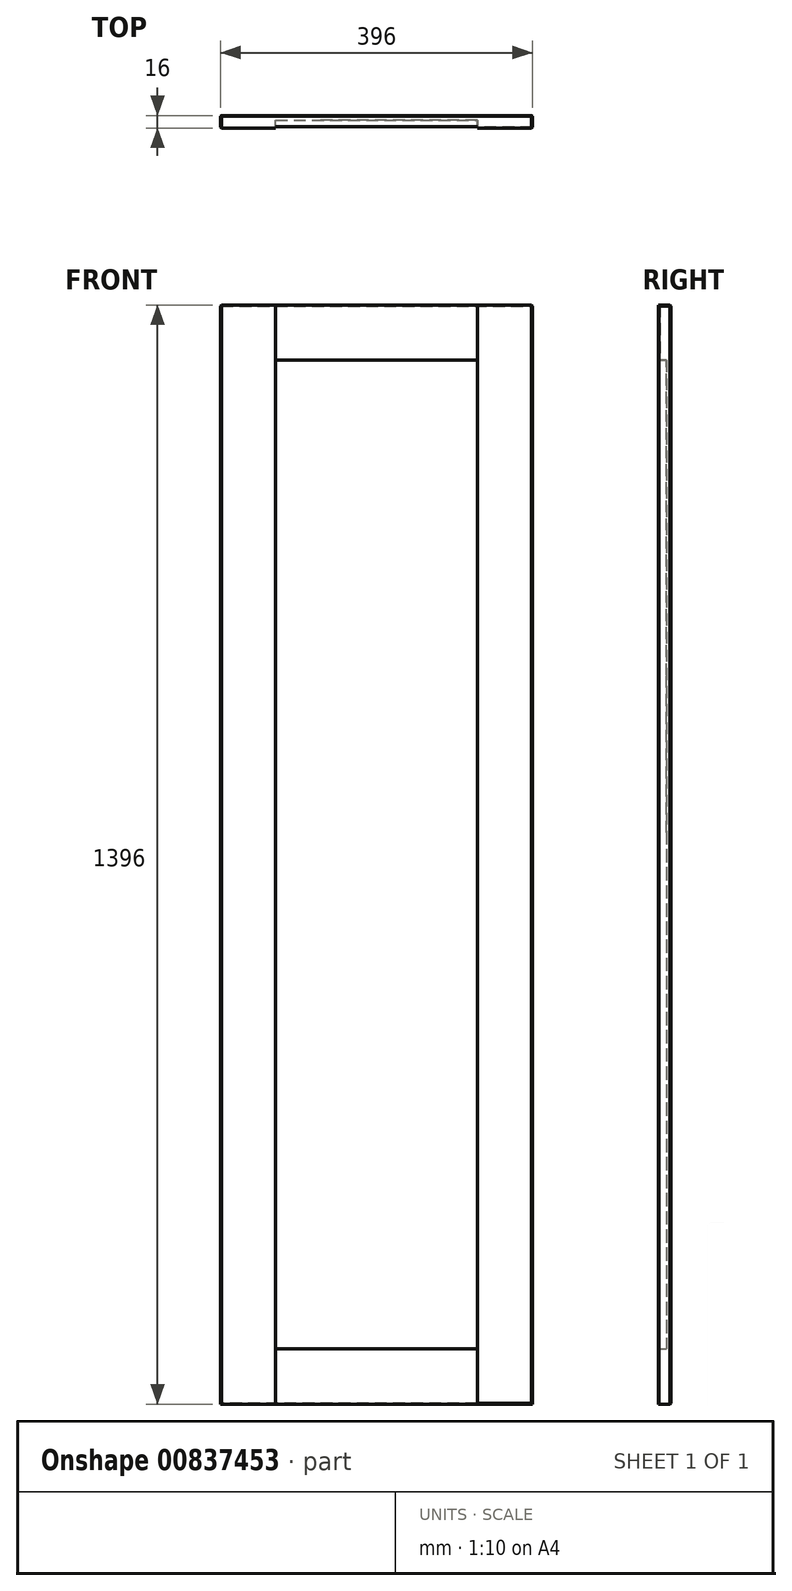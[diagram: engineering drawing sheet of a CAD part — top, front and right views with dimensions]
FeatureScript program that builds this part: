
annotation { "Feature Type Name" : "Feature", "Feature Type Description" : "" }
export const myFeature = defineFeature(function(context is Context, id is Id, definition is map)
    precondition{}
    {
        {
            var Q0;
            Q0=qCreatedBy(makeId("Front.planeOp"),FACE);
            var sketch = newSketch(context, id + "F0", { "sketchPlane" : qUnion([Q0])});
            skLineSegment(sketch, "E0.bottom", {"start": v(0, 0) * mm, "end": v(35.9, 0) * mm});
            skLineSegment(sketch, "E0.top", {"start": v(0, 30.12) * mm, "end": v(35.9, 30.12) * mm});
            skLineSegment(sketch, "E0.left", {"start": v(0, 0) * mm, "end": v(0, 30.12) * mm});
            skLineSegment(sketch, "E0.right", {"start": v(35.9, 0) * mm, "end": v(35.9, 30.12) * mm});
            skSolve(sketch);
        }
        {
            var Q0;
            Q0=makeQuery(id+"F0.imprint","IMPRINT",FACE,{"disambiguationData":[TD([[makeQuery(id+"F0.imprint","IMPRINT",EDGE,{"derivedFrom":sQuery(id+"F0.wireOp",EDGE,"E0.bottom")}),1.0]])]});
            extrude(context, id + "F1", {"entities" : qUnion([Q0]), "depth" : 16 * mm, "offsetDistance" : 25.4 * mm});
        }
        {
            var Q0;
            Q0=makeQuery(id+"F1.opExtrude","SWEPT_FACE",FACE,{"disambiguationData":[OSD([sQuery(id+"F0.wireOp",EDGE,"E0.left")])]});
            extrude(context, id + "F2", {"entities" : qUnion([Q0]), "operationType" : NewBodyOperationType.ADD, "oppositeDirection" : true, "depth" : 196 * mm, "offsetDistance" : 25 * mm});
        }
        {
            var Q0;
            {var subQ0=sQuery(id+"F0.wireOp",EDGE,"E0.bottom");Q0=makeQuery(id+"F2.boolean.opBoolean","MERGE",FACE,{"derivedFrom":[makeQuery(id+"F1.opExtrude","SWEPT_FACE",FACE,{"disambiguationData":[OSD([subQ0])]}),makeQuery(id+"F2.opExtrude","SWEPT_FACE",FACE,{"disambiguationData":[OSD([subQ0,sQuery(id+"F0.wireOp",EDGE,"E0.left")])]})]});}
            extrude(context, id + "F3", {"entities" : qUnion([Q0]), "operationType" : NewBodyOperationType.ADD, "oppositeDirection" : true, "depth" : 796 * mm, "offsetDistance" : 25 * mm});
        }
        {
            var Q0;
            {var subQ0=sQuery(id+"F0.wireOp",EDGE,"E0.left");var subQ1=sQuery(id+"F0.wireOp",EDGE,"E0.bottom");Q0=makeQuery(id+"F3.boolean.opBoolean","MERGE",FACE,{"derivedFrom":[makeQuery(id+"F2.boolean.opBoolean","MERGE",FACE,{"derivedFrom":[makeQuery(id+"F1.opExtrude","CAP_FACE",FACE,{"disambiguationData":[OSD([subQ1,sQuery(id+"F0.wireOp",EDGE,"E0.top"),subQ0,sQuery(id+"F0.wireOp",EDGE,"E0.right")])],"isStart":false}),makeQuery(id+"F2.opExtrude","SWEPT_FACE",FACE,{"disambiguationData":[OSD([subQ0]),TDD([makeQuery(id+"F1.opExtrude","CAP_EDGE",EDGE,{"disambiguationData":[OSD([subQ0])],"isStart":false})])]})]}),makeQuery(id+"F3.opExtrude","SWEPT_FACE",FACE,{"disambiguationData":[OSD([subQ1,subQ0]),TDD([makeQuery(id+"F2.boolean.opBoolean","MERGE",EDGE,{"derivedFrom":[makeQuery(id+"F1.opExtrude","CAP_EDGE",EDGE,{"disambiguationData":[OSD([subQ1])],"isStart":false}),makeQuery(id+"F2.opExtrude","SWEPT_EDGE",EDGE,{"disambiguationData":[OSD([subQ1,subQ0]),TDD([makeQuery(id+"F1.opExtrude","CAP_VERTEX",VERTEX,{"disambiguationData":[OSD([subQ1,subQ0])],"isStart":false})])]})]})])]})]});}
            var sketch = newSketch(context, id + "F4", { "sketchPlane" : qUnion([Q0])});
            skLineSegment(sketch, "E1.bottom", {"start": v(0, 796) * mm, "end": v(42.19, 796) * mm});
            skLineSegment(sketch, "E1.top", {"start": v(0, 751.57) * mm, "end": v(42.19, 751.57) * mm});
            skLineSegment(sketch, "E1.left", {"start": v(0, 796) * mm, "end": v(0, 751.57) * mm});
            skLineSegment(sketch, "E1.right", {"start": v(42.19, 796) * mm, "end": v(42.19, 751.57) * mm});
            skLineSegment(sketch, "E2.bottom", {"start": v(196, 796) * mm, "end": v(153.6, 796) * mm});
            skLineSegment(sketch, "E2.top", {"start": v(196, 746.75) * mm, "end": v(153.6, 746.75) * mm});
            skLineSegment(sketch, "E2.left", {"start": v(196, 796) * mm, "end": v(196, 746.75) * mm});
            skLineSegment(sketch, "E2.right", {"start": v(153.6, 796) * mm, "end": v(153.6, 746.75) * mm});
            skSolve(sketch);
        }
        {
            var Q0;
            Q0=makeQuery(id+"F4.imprint","IMPRINT",FACE,{"disambiguationData":[TD([[makeQuery(id+"F4.imprint","IMPRINT",EDGE,{"derivedFrom":sQuery(id+"F4.wireOp",EDGE,"E1.bottom")}),-1.0]])]});
            var Q1;
            Q1=makeQuery(id+"F4.imprint","IMPRINT",FACE,{"disambiguationData":[TD([[makeQuery(id+"F4.imprint","IMPRINT",EDGE,{"derivedFrom":sQuery(id+"F4.wireOp",EDGE,"E2.bottom")}),-1.0]])]});
            extrude(context, id + "F5", {"entities" : qUnion([Q0, Q1]), "operationType" : NewBodyOperationType.ADD, "depth" : 25 * mm, "offsetDistance" : 25 * mm});
        }
        {
            var Q0;
            {var subQ0=sQuery(id+"F0.wireOp",EDGE,"E0.left");var subQ1=sQuery(id+"F0.wireOp",EDGE,"E0.bottom");Q0=makeQuery(id+"F3.boolean.opBoolean","MERGE",FACE,{"derivedFrom":[makeQuery(id+"F2.boolean.opBoolean","MERGE",FACE,{"derivedFrom":[makeQuery(id+"F1.opExtrude","CAP_FACE",FACE,{"disambiguationData":[OSD([subQ1,sQuery(id+"F0.wireOp",EDGE,"E0.top"),subQ0,sQuery(id+"F0.wireOp",EDGE,"E0.right")])],"isStart":false}),makeQuery(id+"F2.opExtrude","SWEPT_FACE",FACE,{"disambiguationData":[OSD([subQ0]),TDD([makeQuery(id+"F1.opExtrude","CAP_EDGE",EDGE,{"disambiguationData":[OSD([subQ0])],"isStart":false})])]})]}),makeQuery(id+"F3.opExtrude","SWEPT_FACE",FACE,{"disambiguationData":[OSD([subQ1,subQ0]),TDD([makeQuery(id+"F2.boolean.opBoolean","MERGE",EDGE,{"derivedFrom":[makeQuery(id+"F1.opExtrude","CAP_EDGE",EDGE,{"disambiguationData":[OSD([subQ1])],"isStart":false}),makeQuery(id+"F2.opExtrude","SWEPT_EDGE",EDGE,{"disambiguationData":[OSD([subQ1,subQ0]),TDD([makeQuery(id+"F1.opExtrude","CAP_VERTEX",VERTEX,{"disambiguationData":[OSD([subQ1,subQ0])],"isStart":false})])]})]})])]})]});}
            var sketch = newSketch(context, id + "F6", { "sketchPlane" : qUnion([Q0])});
            skLineSegment(sketch, "E3.bottom", {"start": v(196, 0) * mm, "end": v(163.38, 0) * mm});
            skLineSegment(sketch, "E3.top", {"start": v(196, 46.55) * mm, "end": v(163.38, 46.55) * mm});
            skLineSegment(sketch, "E3.left", {"start": v(196, 0) * mm, "end": v(196, 46.55) * mm});
            skLineSegment(sketch, "E3.right", {"start": v(163.38, 0) * mm, "end": v(163.38, 46.55) * mm});
            skLineSegment(sketch, "E4.bottom", {"start": v(0, 0) * mm, "end": v(50.28, 0) * mm});
            skLineSegment(sketch, "E4.top", {"start": v(0, 44.4) * mm, "end": v(50.28, 44.4) * mm});
            skLineSegment(sketch, "E4.left", {"start": v(0, 0) * mm, "end": v(0, 44.4) * mm});
            skLineSegment(sketch, "E4.right", {"start": v(50.28, 0) * mm, "end": v(50.28, 44.4) * mm});
            skSolve(sketch);
        }
        {
            var Q0;
            Q0=makeQuery(id+"F6.imprint","IMPRINT",FACE,{"disambiguationData":[TD([[makeQuery(id+"F6.imprint","IMPRINT",EDGE,{"derivedFrom":sQuery(id+"F6.wireOp",EDGE,"E3.bottom")}),1.0]])]});
            var Q1;
            Q1=makeQuery(id+"F6.imprint","IMPRINT",FACE,{"disambiguationData":[TD([[makeQuery(id+"F6.imprint","IMPRINT",EDGE,{"derivedFrom":sQuery(id+"F6.wireOp",EDGE,"E4.bottom")}),1.0]])]});
            extrude(context, id + "F7", {"entities" : qUnion([Q0, Q1]), "operationType" : NewBodyOperationType.ADD, "depth" : 25 * mm, "offsetDistance" : 25 * mm});
        }
        {
            var Q0;
            Q0=makeQuery(id+"F7.opExtrude","SWEPT_FACE",FACE,{"disambiguationData":[OSD([sQuery(id+"F6.wireOp",EDGE,"E4.right")])]});
            extrude(context, id + "F8", {"entities" : qUnion([Q0]), "operationType" : NewBodyOperationType.ADD, "depth" : 19.72 * mm, "offsetDistance" : 25 * mm});
        }
        {
            var Q0;
            {var subQ0=sQuery(id+"F6.wireOp",EDGE,"E4.top");Q0=makeQuery(id+"F8.boolean.opBoolean","MERGE",FACE,{"derivedFrom":[makeQuery(id+"F7.opExtrude","SWEPT_FACE",FACE,{"disambiguationData":[OSD([subQ0])]}),makeQuery(id+"F8.opExtrude","SWEPT_FACE",FACE,{"disambiguationData":[OSD([subQ0,sQuery(id+"F6.wireOp",EDGE,"E4.right")])]})]});}
            extrude(context, id + "F9", {"entities" : qUnion([Q0]), "operationType" : NewBodyOperationType.ADD, "depth" : 25.6 * mm, "offsetDistance" : 25 * mm});
        }
        {
            var Q0;
            Q0=makeQuery(id+"F7.opExtrude","SWEPT_FACE",FACE,{"disambiguationData":[OSD([sQuery(id+"F6.wireOp",EDGE,"E3.right")])]});
            extrude(context, id + "F10", {"entities" : qUnion([Q0]), "operationType" : NewBodyOperationType.ADD, "depth" : 37.38 * mm, "offsetDistance" : 25 * mm});
        }
        {
            var Q0;
            {var subQ0=sQuery(id+"F6.wireOp",EDGE,"E3.top");Q0=makeQuery(id+"F10.boolean.opBoolean","MERGE",FACE,{"derivedFrom":[makeQuery(id+"F7.opExtrude","SWEPT_FACE",FACE,{"disambiguationData":[OSD([subQ0])]}),makeQuery(id+"F10.opExtrude","SWEPT_FACE",FACE,{"disambiguationData":[OSD([subQ0,sQuery(id+"F6.wireOp",EDGE,"E3.right")])]})]});}
            extrude(context, id + "F11", {"entities" : qUnion([Q0]), "operationType" : NewBodyOperationType.ADD, "depth" : 23.45 * mm, "offsetDistance" : 25 * mm});
        }
        {
            var Q0;
            Q0=makeQuery(id+"F5.opExtrude","SWEPT_FACE",FACE,{"disambiguationData":[OSD([sQuery(id+"F4.wireOp",EDGE,"E1.right")])]});
            extrude(context, id + "F12", {"entities" : qUnion([Q0]), "operationType" : NewBodyOperationType.ADD, "depth" : 27.8 * mm, "offsetDistance" : 25 * mm});
        }
        {
            var Q0;
            {var subQ0=sQuery(id+"F4.wireOp",EDGE,"E1.top");Q0=makeQuery(id+"F12.boolean.opBoolean","MERGE",FACE,{"derivedFrom":[makeQuery(id+"F5.opExtrude","SWEPT_FACE",FACE,{"disambiguationData":[OSD([subQ0])]}),makeQuery(id+"F12.opExtrude","SWEPT_FACE",FACE,{"disambiguationData":[OSD([subQ0,sQuery(id+"F4.wireOp",EDGE,"E1.right")])]})]});}
            extrude(context, id + "F13", {"entities" : qUnion([Q0]), "operationType" : NewBodyOperationType.ADD, "depth" : 25.57 * mm, "offsetDistance" : 25 * mm});
        }
        {
            var Q0;
            Q0=makeQuery(id+"F5.opExtrude","SWEPT_FACE",FACE,{"disambiguationData":[OSD([sQuery(id+"F4.wireOp",EDGE,"E2.top")])]});
            extrude(context, id + "F14", {"entities" : qUnion([Q0]), "operationType" : NewBodyOperationType.ADD, "depth" : 20.75 * mm, "offsetDistance" : 25 * mm});
        }
        {
            var Q0;
            {var subQ0=sQuery(id+"F4.wireOp",EDGE,"E2.right");Q0=makeQuery(id+"F14.boolean.opBoolean","MERGE",FACE,{"derivedFrom":[makeQuery(id+"F5.opExtrude","SWEPT_FACE",FACE,{"disambiguationData":[OSD([subQ0])]}),makeQuery(id+"F14.opExtrude","SWEPT_FACE",FACE,{"disambiguationData":[OSD([sQuery(id+"F4.wireOp",EDGE,"E2.top"),subQ0])]})]});}
            extrude(context, id + "F15", {"entities" : qUnion([Q0]), "operationType" : NewBodyOperationType.ADD, "depth" : 27.6 * mm, "offsetDistance" : 25 * mm});
        }
        {
            var Q0;
            {var subQ0=sQuery(id+"F0.wireOp",EDGE,"E0.left");var subQ1=sQuery(id+"F0.wireOp",EDGE,"E0.bottom");Q0=makeQuery(id+"F3.boolean.opBoolean","MERGE",FACE,{"derivedFrom":[makeQuery(id+"F2.boolean.opBoolean","MERGE",FACE,{"derivedFrom":[makeQuery(id+"F1.opExtrude","CAP_FACE",FACE,{"disambiguationData":[OSD([subQ1,sQuery(id+"F0.wireOp",EDGE,"E0.top"),subQ0,sQuery(id+"F0.wireOp",EDGE,"E0.right")])],"isStart":false}),makeQuery(id+"F2.opExtrude","SWEPT_FACE",FACE,{"disambiguationData":[OSD([subQ0]),TDD([makeQuery(id+"F1.opExtrude","CAP_EDGE",EDGE,{"disambiguationData":[OSD([subQ0])],"isStart":false})])]})]}),makeQuery(id+"F3.opExtrude","SWEPT_FACE",FACE,{"disambiguationData":[OSD([subQ1,subQ0]),TDD([makeQuery(id+"F2.boolean.opBoolean","MERGE",EDGE,{"derivedFrom":[makeQuery(id+"F1.opExtrude","CAP_EDGE",EDGE,{"disambiguationData":[OSD([subQ1])],"isStart":false}),makeQuery(id+"F2.opExtrude","SWEPT_EDGE",EDGE,{"disambiguationData":[OSD([subQ1,subQ0]),TDD([makeQuery(id+"F1.opExtrude","CAP_VERTEX",VERTEX,{"disambiguationData":[OSD([subQ1,subQ0])],"isStart":false})])]})]})])]})]});}
            var sketch = newSketch(context, id + "F16", { "sketchPlane" : qUnion([Q0])});
            skLineSegment(sketch, "E5.bottom", {"start": v(70, 726) * mm, "end": v(126, 726) * mm});
            skLineSegment(sketch, "E5.top", {"start": v(70, 70) * mm, "end": v(126, 70) * mm});
            skLineSegment(sketch, "E5.left", {"start": v(70, 726) * mm, "end": v(70, 70) * mm});
            skLineSegment(sketch, "E5.right", {"start": v(126, 726) * mm, "end": v(126, 70) * mm});
            skSolve(sketch);
        }
        {
            var Q0;
            Q0=makeQuery(id+"F16.imprint","IMPRINT",FACE,{"disambiguationData":[TD([[makeQuery(id+"F16.imprint","IMPRINT",EDGE,{"derivedFrom":sQuery(id+"F16.wireOp",EDGE,"E5.top")}),1.0]])]});
            extrude(context, id + "F17", {"entities" : qUnion([Q0]), "operationType" : NewBodyOperationType.REMOVE, "oppositeDirection" : true, "depth" : 10 * mm, "offsetDistance" : 25 * mm});
        }
        {
            var Q0;
            {var subQ2=sQuery(id+"F0.wireOp",EDGE,"E0.left");var subQ3=sQuery(id+"F0.wireOp",EDGE,"E0.bottom");var subQ4=makeQuery(id+"F1.opExtrude","CAP_FACE",FACE,{"disambiguationData":[OSD([subQ3,sQuery(id+"F0.wireOp",EDGE,"E0.top"),subQ2,sQuery(id+"F0.wireOp",EDGE,"E0.right")])],"isStart":false});var subQ7=makeQuery(id+"F3.opExtrude","SWEPT_FACE",FACE,{"disambiguationData":[OSD([subQ3,subQ2]),TDD([makeQuery(id+"F2.boolean.opBoolean","MERGE",EDGE,{"derivedFrom":[makeQuery(id+"F1.opExtrude","CAP_EDGE",EDGE,{"disambiguationData":[OSD([subQ3])],"isStart":false}),makeQuery(id+"F2.opExtrude","SWEPT_EDGE",EDGE,{"disambiguationData":[OSD([subQ3,subQ2]),TDD([makeQuery(id+"F1.opExtrude","CAP_VERTEX",VERTEX,{"disambiguationData":[OSD([subQ3,subQ2])],"isStart":false})])]})]})])]});var subQ8=makeQuery(id+"F2.opExtrude","SWEPT_FACE",FACE,{"disambiguationData":[OSD([subQ2]),TDD([makeQuery(id+"F1.opExtrude","CAP_EDGE",EDGE,{"disambiguationData":[OSD([subQ2])],"isStart":false})])]});Q0=makeQuery(id+"F17.boolean.opBoolean","SPLIT",FACE,{"disambiguationData":[TD([makeQuery(id+"F1.opExtrude","SWEPT_FACE",FACE,{"disambiguationData":[OSD([subQ3])]})])],"derivedFrom":makeQuery(id+"F3.boolean.opBoolean","MERGE",FACE,{"derivedFrom":[makeQuery(id+"F2.boolean.opBoolean","MERGE",FACE,{"derivedFrom":[subQ4,subQ8]}),subQ7]})});}
            var Q1;
            {var subQ2=sQuery(id+"F4.wireOp",EDGE,"E1.bottom");var subQ3=sQuery(id+"F0.wireOp",EDGE,"E0.left");var subQ4=sQuery(id+"F0.wireOp",EDGE,"E0.bottom");var subQ6=makeQuery(id+"F1.opExtrude","CAP_FACE",FACE,{"disambiguationData":[OSD([subQ4,sQuery(id+"F0.wireOp",EDGE,"E0.top"),subQ3,sQuery(id+"F0.wireOp",EDGE,"E0.right")])],"isStart":false});var subQ7=makeQuery(id+"F2.opExtrude","SWEPT_FACE",FACE,{"disambiguationData":[OSD([subQ3]),TDD([makeQuery(id+"F1.opExtrude","CAP_EDGE",EDGE,{"disambiguationData":[OSD([subQ3])],"isStart":false})])]});var subQ8=makeQuery(id+"F3.opExtrude","SWEPT_FACE",FACE,{"disambiguationData":[OSD([subQ4,subQ3]),TDD([makeQuery(id+"F2.boolean.opBoolean","MERGE",EDGE,{"derivedFrom":[makeQuery(id+"F1.opExtrude","CAP_EDGE",EDGE,{"disambiguationData":[OSD([subQ4])],"isStart":false}),makeQuery(id+"F2.opExtrude","SWEPT_EDGE",EDGE,{"disambiguationData":[OSD([subQ4,subQ3]),TDD([makeQuery(id+"F1.opExtrude","CAP_VERTEX",VERTEX,{"disambiguationData":[OSD([subQ4,subQ3])],"isStart":false})])]})]})])]});Q1=makeQuery(id+"F17.boolean.opBoolean","SPLIT",FACE,{"disambiguationData":[TD([makeQuery(id+"F5.opExtrude","SWEPT_FACE",FACE,{"disambiguationData":[OSD([subQ2])]})])],"derivedFrom":makeQuery(id+"F3.boolean.opBoolean","MERGE",FACE,{"derivedFrom":[makeQuery(id+"F2.boolean.opBoolean","MERGE",FACE,{"derivedFrom":[subQ6,subQ7]}),subQ8]})});}
            extrude(context, id + "F18", {"entities" : qUnion([Q0, Q1]), "operationType" : NewBodyOperationType.REMOVE, "oppositeDirection" : true, "depth" : 2 * mm, "offsetDistance" : 25 * mm});
        }
        {
            var Q0;
            {var subQ0=sQuery(id+"F4.wireOp",EDGE,"E1.right");var subQ1=sQuery(id+"F4.wireOp",EDGE,"E1.top");Q0=makeQuery(id+"F13.boolean.opBoolean","MERGE",FACE,{"derivedFrom":[makeQuery(id+"F12.boolean.opBoolean","MERGE",FACE,{"derivedFrom":[makeQuery(id+"F5.opExtrude","CAP_FACE",FACE,{"disambiguationData":[OSD([sQuery(id+"F4.wireOp",EDGE,"E1.bottom"),subQ1,sQuery(id+"F4.wireOp",EDGE,"E1.left"),subQ0])],"isStart":false}),makeQuery(id+"F12.opExtrude","SWEPT_FACE",FACE,{"disambiguationData":[OSD([subQ0]),TDD([makeQuery(id+"F5.opExtrude","CAP_EDGE",EDGE,{"disambiguationData":[OSD([subQ0])],"isStart":false})])]})]}),makeQuery(id+"F13.opExtrude","SWEPT_FACE",FACE,{"disambiguationData":[OSD([subQ1,subQ0]),TDD([makeQuery(id+"F12.boolean.opBoolean","MERGE",EDGE,{"derivedFrom":[makeQuery(id+"F5.opExtrude","CAP_EDGE",EDGE,{"disambiguationData":[OSD([subQ1])],"isStart":false}),makeQuery(id+"F12.opExtrude","SWEPT_EDGE",EDGE,{"disambiguationData":[OSD([subQ1,subQ0]),TDD([makeQuery(id+"F5.opExtrude","CAP_VERTEX",VERTEX,{"disambiguationData":[OSD([subQ1,subQ0])],"isStart":false})])]})]})])]})]});}
            var Q1;
            {var subQ0=sQuery(id+"F4.wireOp",EDGE,"E2.right");var subQ1=sQuery(id+"F4.wireOp",EDGE,"E2.top");Q1=makeQuery(id+"F15.boolean.opBoolean","MERGE",FACE,{"derivedFrom":[makeQuery(id+"F14.boolean.opBoolean","MERGE",FACE,{"derivedFrom":[makeQuery(id+"F5.opExtrude","CAP_FACE",FACE,{"disambiguationData":[OSD([sQuery(id+"F4.wireOp",EDGE,"E2.bottom"),subQ1,sQuery(id+"F4.wireOp",EDGE,"E2.left"),subQ0])],"isStart":false}),makeQuery(id+"F14.opExtrude","SWEPT_FACE",FACE,{"disambiguationData":[OSD([subQ1]),TDD([makeQuery(id+"F5.opExtrude","CAP_EDGE",EDGE,{"disambiguationData":[OSD([subQ1])],"isStart":false})])]})]}),makeQuery(id+"F15.opExtrude","SWEPT_FACE",FACE,{"disambiguationData":[OSD([subQ1,subQ0]),TDD([makeQuery(id+"F14.boolean.opBoolean","MERGE",EDGE,{"derivedFrom":[makeQuery(id+"F5.opExtrude","CAP_EDGE",EDGE,{"disambiguationData":[OSD([subQ0])],"isStart":false}),makeQuery(id+"F14.opExtrude","SWEPT_EDGE",EDGE,{"disambiguationData":[OSD([subQ1,subQ0]),TDD([makeQuery(id+"F5.opExtrude","CAP_VERTEX",VERTEX,{"disambiguationData":[OSD([subQ1,subQ0])],"isStart":false})])]})]})])]})]});}
            var Q2;
            {var subQ0=sQuery(id+"F6.wireOp",EDGE,"E4.right");var subQ1=sQuery(id+"F6.wireOp",EDGE,"E4.top");Q2=makeQuery(id+"F9.boolean.opBoolean","MERGE",FACE,{"derivedFrom":[makeQuery(id+"F8.boolean.opBoolean","MERGE",FACE,{"derivedFrom":[makeQuery(id+"F7.opExtrude","CAP_FACE",FACE,{"disambiguationData":[OSD([sQuery(id+"F6.wireOp",EDGE,"E4.bottom"),subQ1,sQuery(id+"F6.wireOp",EDGE,"E4.left"),subQ0])],"isStart":false}),makeQuery(id+"F8.opExtrude","SWEPT_FACE",FACE,{"disambiguationData":[OSD([subQ0]),TDD([makeQuery(id+"F7.opExtrude","CAP_EDGE",EDGE,{"disambiguationData":[OSD([subQ0])],"isStart":false})])]})]}),makeQuery(id+"F9.opExtrude","SWEPT_FACE",FACE,{"disambiguationData":[OSD([subQ1,subQ0]),TDD([makeQuery(id+"F8.boolean.opBoolean","MERGE",EDGE,{"derivedFrom":[makeQuery(id+"F7.opExtrude","CAP_EDGE",EDGE,{"disambiguationData":[OSD([subQ1])],"isStart":false}),makeQuery(id+"F8.opExtrude","SWEPT_EDGE",EDGE,{"disambiguationData":[OSD([subQ1,subQ0]),TDD([makeQuery(id+"F7.opExtrude","CAP_VERTEX",VERTEX,{"disambiguationData":[OSD([subQ1,subQ0])],"isStart":false})])]})]})])]})]});}
            var Q3;
            {var subQ0=sQuery(id+"F6.wireOp",EDGE,"E3.right");var subQ1=sQuery(id+"F6.wireOp",EDGE,"E3.top");Q3=makeQuery(id+"F11.boolean.opBoolean","MERGE",FACE,{"derivedFrom":[makeQuery(id+"F10.boolean.opBoolean","MERGE",FACE,{"derivedFrom":[makeQuery(id+"F7.opExtrude","CAP_FACE",FACE,{"disambiguationData":[OSD([sQuery(id+"F6.wireOp",EDGE,"E3.bottom"),subQ1,sQuery(id+"F6.wireOp",EDGE,"E3.left"),subQ0])],"isStart":false}),makeQuery(id+"F10.opExtrude","SWEPT_FACE",FACE,{"disambiguationData":[OSD([subQ0]),TDD([makeQuery(id+"F7.opExtrude","CAP_EDGE",EDGE,{"disambiguationData":[OSD([subQ0])],"isStart":false})])]})]}),makeQuery(id+"F11.opExtrude","SWEPT_FACE",FACE,{"disambiguationData":[OSD([subQ1,subQ0]),TDD([makeQuery(id+"F10.boolean.opBoolean","MERGE",EDGE,{"derivedFrom":[makeQuery(id+"F7.opExtrude","CAP_EDGE",EDGE,{"disambiguationData":[OSD([subQ1])],"isStart":false}),makeQuery(id+"F10.opExtrude","SWEPT_EDGE",EDGE,{"disambiguationData":[OSD([subQ1,subQ0]),TDD([makeQuery(id+"F7.opExtrude","CAP_VERTEX",VERTEX,{"disambiguationData":[OSD([subQ1,subQ0])],"isStart":false})])]})]})])]})]});}
            extrude(context, id + "F19", {"entities" : qUnion([Q0, Q1, Q2, Q3]), "operationType" : NewBodyOperationType.REMOVE, "oppositeDirection" : true, "depth" : 25 * mm, "offsetDistance" : 25 * mm});
        }
        {
            var Q0;
            {var subQ0=sQuery(id+"F4.wireOp",EDGE,"E2.left");var subQ1=sQuery(id+"F0.wireOp",EDGE,"E0.left");var subQ2=sQuery(id+"F0.wireOp",EDGE,"E0.bottom");var subQ3=sQuery(id+"F6.wireOp",EDGE,"E3.left");Q0=makeQuery(id+"F14.boolean.opBoolean","MERGE",FACE,{"derivedFrom":[makeQuery(id+"F11.boolean.opBoolean","MERGE",FACE,{"derivedFrom":[makeQuery(id+"F7.boolean.opBoolean","MERGE",FACE,{"derivedFrom":[makeQuery(id+"F5.boolean.opBoolean","MERGE",FACE,{"derivedFrom":[makeQuery(id+"F3.boolean.opBoolean","MERGE",FACE,{"derivedFrom":[makeQuery(id+"F2.opExtrude","CAP_FACE",FACE,{"disambiguationData":[OSD([subQ1])],"isStart":false}),makeQuery(id+"F3.opExtrude","SWEPT_FACE",FACE,{"disambiguationData":[OSD([subQ2,subQ1]),TDD([makeQuery(id+"F2.opExtrude","CAP_EDGE",EDGE,{"disambiguationData":[OSD([subQ2,subQ1])],"isStart":false})])]})]}),makeQuery(id+"F5.opExtrude","SWEPT_FACE",FACE,{"disambiguationData":[OSD([subQ0])]})]}),makeQuery(id+"F7.opExtrude","SWEPT_FACE",FACE,{"disambiguationData":[OSD([subQ3])]})]}),makeQuery(id+"F11.opExtrude","SWEPT_FACE",FACE,{"disambiguationData":[OSD([subQ2,subQ1,sQuery(id+"F6.wireOp",EDGE,"E3.top"),subQ3])]})]}),makeQuery(id+"F14.opExtrude","SWEPT_FACE",FACE,{"disambiguationData":[OSD([subQ2,subQ1,sQuery(id+"F4.wireOp",EDGE,"E2.top"),subQ0])]})]});}
            extrude(context, id + "F20", {"entities" : qUnion([Q0]), "operationType" : NewBodyOperationType.ADD, "depth" : 200 * mm, "offsetDistance" : 25 * mm});
        }
        {
            var Q0;
            {var subQ0=sQuery(id+"F4.wireOp",EDGE,"E2.right");var subQ1=sQuery(id+"F4.wireOp",EDGE,"E2.top");Q0=makeQuery(id+"F18.boolean.opBoolean","MERGE",FACE,{"derivedFrom":[makeQuery(id+"F15.opExtrude","CAP_FACE",FACE,{"disambiguationData":[OSD([subQ1,subQ0])],"isStart":false}),makeQuery(id+"F18.opExtrude","SWEPT_FACE",FACE,{"disambiguationData":[OSD([subQ1,subQ0])]})]});}
            var Q1;
            {var subQ0=sQuery(id+"F6.wireOp",EDGE,"E3.right");var subQ1=sQuery(id+"F6.wireOp",EDGE,"E3.top");Q1=makeQuery(id+"F18.boolean.opBoolean","MERGE",FACE,{"derivedFrom":[makeQuery(id+"F11.boolean.opBoolean","MERGE",FACE,{"derivedFrom":[makeQuery(id+"F10.opExtrude","CAP_FACE",FACE,{"disambiguationData":[OSD([subQ0])],"isStart":false}),makeQuery(id+"F11.opExtrude","SWEPT_FACE",FACE,{"disambiguationData":[OSD([subQ1,subQ0]),TDD([makeQuery(id+"F10.opExtrude","CAP_EDGE",EDGE,{"disambiguationData":[OSD([subQ1,subQ0])],"isStart":false})])]})]}),makeQuery(id+"F17.boolean.opBoolean","COPY",FACE,{"derivedFrom":makeQuery(id+"F17.opExtrude","SWEPT_FACE",FACE,{"disambiguationData":[OSD([sQuery(id+"F16.wireOp",EDGE,"E5.right")])]})}),makeQuery(id+"F18.opExtrude","SWEPT_FACE",FACE,{"disambiguationData":[OSD([subQ1,subQ0])]})]});}
            extrude(context, id + "F21", {"entities" : qUnion([Q0, Q1]), "operationType" : NewBodyOperationType.REMOVE, "oppositeDirection" : true, "depth" : 200 * mm, "offsetDistance" : 25 * mm});
        }
        {
            var Q0;
            {var subQ0=sQuery(id+"F4.wireOp",EDGE,"E2.bottom");var subQ1=sQuery(id+"F0.wireOp",EDGE,"E0.left");var subQ2=sQuery(id+"F0.wireOp",EDGE,"E0.bottom");var subQ3=sQuery(id+"F4.wireOp",EDGE,"E1.bottom");Q0=makeQuery(id+"F20.boolean.opBoolean","MERGE",FACE,{"derivedFrom":[makeQuery(id+"F15.boolean.opBoolean","MERGE",FACE,{"derivedFrom":[makeQuery(id+"F12.boolean.opBoolean","MERGE",FACE,{"derivedFrom":[makeQuery(id+"F5.boolean.opBoolean","MERGE",FACE,{"derivedFrom":[makeQuery(id+"F3.opExtrude","CAP_FACE",FACE,{"disambiguationData":[OSD([subQ2,subQ1])],"isStart":false}),makeQuery(id+"F5.opExtrude","SWEPT_FACE",FACE,{"disambiguationData":[OSD([subQ3])]}),makeQuery(id+"F5.opExtrude","SWEPT_FACE",FACE,{"disambiguationData":[OSD([subQ0])]})]}),makeQuery(id+"F12.opExtrude","SWEPT_FACE",FACE,{"disambiguationData":[OSD([subQ2,subQ1,subQ3,sQuery(id+"F4.wireOp",EDGE,"E1.right")])]})]}),makeQuery(id+"F15.opExtrude","SWEPT_FACE",FACE,{"disambiguationData":[OSD([subQ2,subQ1,subQ0,sQuery(id+"F4.wireOp",EDGE,"E2.right")])]})]}),makeQuery(id+"F20.opExtrude","SWEPT_FACE",FACE,{"disambiguationData":[OSD([subQ2,subQ1,subQ0,sQuery(id+"F4.wireOp",EDGE,"E2.left")])]})]});}
            extrude(context, id + "F22", {"entities" : qUnion([Q0]), "operationType" : NewBodyOperationType.ADD, "depth" : 200 * mm, "offsetDistance" : 25 * mm});
        }
        {
            var Q0;
            Q0=makeQuery(id+"F17.boolean.opBoolean","COPY",FACE,{"derivedFrom":makeQuery(id+"F17.opExtrude","SWEPT_FACE",FACE,{"disambiguationData":[OSD([sQuery(id+"F16.wireOp",EDGE,"E5.bottom")])]})});
            var Q1;
            {var subQ0=sQuery(id+"F16.wireOp",EDGE,"E5.right");var subQ1=sQuery(id+"F16.wireOp",EDGE,"E5.bottom");var subQ2=sQuery(id+"F4.wireOp",EDGE,"E2.right");var subQ3=sQuery(id+"F4.wireOp",EDGE,"E2.top");var subQ4=makeQuery(id+"F17.boolean.opBoolean","COPY",EDGE,{"derivedFrom":makeQuery(id+"F17.opExtrude","SWEPT_EDGE",EDGE,{"disambiguationData":[OSD([subQ3,subQ2,subQ1,subQ0])]})});Q1=makeQuery(id+"F21.boolean.opBoolean","COPY",FACE,{"derivedFrom":makeQuery(id+"F21.opExtrude","SWEPT_FACE",FACE,{"disambiguationData":[OSD([subQ3,subQ2,subQ1,subQ0]),TDD([makeQuery(id+"F18.boolean.opBoolean","MERGE",EDGE,{"derivedFrom":[subQ4,makeQuery(id+"F18.opExtrude","SWEPT_EDGE",EDGE,{"disambiguationData":[OSD([subQ3,subQ2,subQ1,subQ0])]})]}),makeQuery(id+"F18.boolean.opBoolean","SPLIT",EDGE,{"derivedFrom":subQ4})])]})});}
            extrude(context, id + "F23", {"entities" : qUnion([Q0, Q1]), "operationType" : NewBodyOperationType.REMOVE, "oppositeDirection" : true, "depth" : 200 * mm, "offsetDistance" : 25 * mm});
        }
        {
            var Q0;
            Q0=makeQuery(id+"F22.opExtrude","CAP_FACE",FACE,{"disambiguationData":[OSD([sQuery(id+"F0.wireOp",EDGE,"E0.bottom"),sQuery(id+"F0.wireOp",EDGE,"E0.left"),sQuery(id+"F4.wireOp",EDGE,"E1.bottom"),sQuery(id+"F4.wireOp",EDGE,"E1.right"),sQuery(id+"F4.wireOp",EDGE,"E2.bottom"),sQuery(id+"F4.wireOp",EDGE,"E2.left"),sQuery(id+"F4.wireOp",EDGE,"E2.right")])],"isStart":false});
            extrude(context, id + "F24", {"entities" : qUnion([Q0]), "operationType" : NewBodyOperationType.ADD, "depth" : 400 * mm, "offsetDistance" : 25 * mm});
        }
        {
            var Q0;
            Q0=makeQuery(id+"F23.boolean.opBoolean","COPY",FACE,{"derivedFrom":makeQuery(id+"F23.opExtrude","CAP_FACE",FACE,{"disambiguationData":[OSD([sQuery(id+"F4.wireOp",EDGE,"E2.top"),sQuery(id+"F4.wireOp",EDGE,"E2.right"),sQuery(id+"F16.wireOp",EDGE,"E5.bottom"),sQuery(id+"F16.wireOp",EDGE,"E5.right")])],"isStart":false})});
            var Q1;
            Q1=makeQuery(id+"F23.boolean.opBoolean","COPY",FACE,{"derivedFrom":makeQuery(id+"F23.opExtrude","CAP_FACE",FACE,{"disambiguationData":[OSD([sQuery(id+"F16.wireOp",EDGE,"E5.bottom")])],"isStart":false})});
            extrude(context, id + "F25", {"entities" : qUnion([Q0, Q1]), "operationType" : NewBodyOperationType.REMOVE, "oppositeDirection" : true, "depth" : 400 * mm, "offsetDistance" : 25 * mm});
        }
        {
            var Q0;
            Q0=makeQuery(id+"F24.opExtrude","CAP_EDGE",EDGE,{"disambiguationData":[OSD([sQuery(id+"F0.wireOp",EDGE,"E0.bottom"),sQuery(id+"F0.wireOp",EDGE,"E0.left"),sQuery(id+"F4.wireOp",EDGE,"E2.bottom"),sQuery(id+"F4.wireOp",EDGE,"E2.left"),sQuery(id+"F4.wireOp",EDGE,"E2.right")])],"isStart":false});
            var Q1;
            {var subQ0=sQuery(id+"F4.wireOp",EDGE,"E2.left");var subQ1=sQuery(id+"F4.wireOp",EDGE,"E2.bottom");Q1=makeQuery(id+"F24.boolean.opBoolean","MERGE",EDGE,{"derivedFrom":[makeQuery(id+"F22.boolean.opBoolean","MERGE",EDGE,{"derivedFrom":[makeQuery(id+"F20.opExtrude","CAP_EDGE",EDGE,{"disambiguationData":[OSD([sQuery(id+"F0.wireOp",EDGE,"E0.bottom"),sQuery(id+"F0.wireOp",EDGE,"E0.left"),sQuery(id+"F4.wireOp",EDGE,"E2.top"),subQ0,sQuery(id+"F6.wireOp",EDGE,"E3.top"),sQuery(id+"F6.wireOp",EDGE,"E3.left")])],"isStart":false}),makeQuery(id+"F22.opExtrude","SWEPT_EDGE",EDGE,{"disambiguationData":[OSD([subQ1,subQ0])]})]}),makeQuery(id+"F24.opExtrude","SWEPT_EDGE",EDGE,{"disambiguationData":[OSD([subQ1,subQ0])]})]});}
            var Q2;
            {var subQ0=sQuery(id+"F4.wireOp",EDGE,"E1.right");var subQ1=sQuery(id+"F4.wireOp",EDGE,"E1.bottom");var subQ2=sQuery(id+"F0.wireOp",EDGE,"E0.left");var subQ3=sQuery(id+"F0.wireOp",EDGE,"E0.bottom");Q2=makeQuery(id+"F24.opExtrude","CAP_EDGE",EDGE,{"disambiguationData":[OSD([subQ3,subQ2,subQ1,subQ0]),TDD([makeQuery(id+"F22.opExtrude","CAP_EDGE",EDGE,{"disambiguationData":[OSD([subQ3,subQ2,subQ1,subQ0]),TDD([makeQuery(id+"F19.boolean.opBoolean","COPY",EDGE,{"derivedFrom":makeQuery(id+"F19.opExtrude","CAP_EDGE",EDGE,{"disambiguationData":[OSD([subQ3,subQ2,subQ1,subQ0])],"isStart":false})})])],"isStart":false})])],"isStart":false});}
            var Q3;
            {var subQ0=sQuery(id+"F4.wireOp",EDGE,"E1.left");var subQ1=sQuery(id+"F4.wireOp",EDGE,"E1.bottom");var subQ2=sQuery(id+"F0.wireOp",EDGE,"E0.left");var subQ3=sQuery(id+"F0.wireOp",EDGE,"E0.bottom");Q3=makeQuery(id+"F24.boolean.opBoolean","MERGE",EDGE,{"derivedFrom":[makeQuery(id+"F22.boolean.opBoolean","MERGE",EDGE,{"derivedFrom":[makeQuery(id+"F19.boolean.opBoolean","MERGE",EDGE,{"derivedFrom":[makeQuery(id+"F3.boolean.opBoolean","MERGE",EDGE,{"derivedFrom":[makeQuery(id+"F1.opExtrude","CAP_EDGE",EDGE,{"disambiguationData":[OSD([subQ2])],"isStart":false}),makeQuery(id+"F3.opExtrude","SWEPT_EDGE",EDGE,{"disambiguationData":[OSD([subQ3,subQ2]),TDD([makeQuery(id+"F1.opExtrude","CAP_VERTEX",VERTEX,{"disambiguationData":[OSD([subQ3,subQ2])],"isStart":false})])]})]}),makeQuery(id+"F19.opExtrude","CAP_EDGE",EDGE,{"disambiguationData":[OSD([subQ3,subQ2,sQuery(id+"F6.wireOp",EDGE,"E4.top"),sQuery(id+"F6.wireOp",EDGE,"E4.left")])],"isStart":false}),makeQuery(id+"F19.opExtrude","CAP_EDGE",EDGE,{"disambiguationData":[OSD([subQ3,subQ2,sQuery(id+"F4.wireOp",EDGE,"E1.top"),subQ0])],"isStart":false})]}),makeQuery(id+"F22.opExtrude","SWEPT_EDGE",EDGE,{"disambiguationData":[OSD([subQ1,subQ0])]})]}),makeQuery(id+"F24.opExtrude","SWEPT_EDGE",EDGE,{"disambiguationData":[OSD([subQ1,subQ0])]})]});}
            var Q4;
            Q4=makeQuery(id+"F19.boolean.opBoolean","COPY",EDGE,{"derivedFrom":makeQuery(id+"F19.opExtrude","CAP_EDGE",EDGE,{"disambiguationData":[OSD([sQuery(id+"F0.wireOp",EDGE,"E0.bottom"),sQuery(id+"F0.wireOp",EDGE,"E0.left"),sQuery(id+"F6.wireOp",EDGE,"E4.bottom"),sQuery(id+"F6.wireOp",EDGE,"E4.right")])],"isStart":false})});
            var Q5;
            {var subQ0=sQuery(id+"F6.wireOp",EDGE,"E3.bottom");Q5=makeQuery(id+"F20.boolean.opBoolean","MERGE",EDGE,{"derivedFrom":[makeQuery(id+"F19.boolean.opBoolean","COPY",EDGE,{"derivedFrom":makeQuery(id+"F19.opExtrude","CAP_EDGE",EDGE,{"disambiguationData":[OSD([sQuery(id+"F0.wireOp",EDGE,"E0.bottom"),sQuery(id+"F0.wireOp",EDGE,"E0.left"),subQ0,sQuery(id+"F6.wireOp",EDGE,"E3.right")])],"isStart":false})}),makeQuery(id+"F20.opExtrude","SWEPT_EDGE",EDGE,{"disambiguationData":[OSD([subQ0,sQuery(id+"F6.wireOp",EDGE,"E3.left")])]})]});}
            var Q6;
            {var subQ0=sQuery(id+"F0.wireOp",EDGE,"E0.left");var subQ1=sQuery(id+"F0.wireOp",EDGE,"E0.bottom");Q6=makeQuery(id+"F24.boolean.opBoolean","MERGE",FACE,{"derivedFrom":[makeQuery(id+"F22.boolean.opBoolean","MERGE",FACE,{"derivedFrom":[makeQuery(id+"F20.boolean.opBoolean","MERGE",FACE,{"derivedFrom":[makeQuery(id+"F3.boolean.opBoolean","MERGE",FACE,{"derivedFrom":[makeQuery(id+"F2.boolean.opBoolean","MERGE",FACE,{"derivedFrom":[makeQuery(id+"F1.opExtrude","CAP_FACE",FACE,{"disambiguationData":[OSD([subQ1,sQuery(id+"F0.wireOp",EDGE,"E0.top"),subQ0,sQuery(id+"F0.wireOp",EDGE,"E0.right")])],"isStart":true}),makeQuery(id+"F2.opExtrude","SWEPT_FACE",FACE,{"disambiguationData":[OSD([subQ0]),TDD([makeQuery(id+"F1.opExtrude","CAP_EDGE",EDGE,{"disambiguationData":[OSD([subQ0])],"isStart":true})])]})]}),makeQuery(id+"F3.opExtrude","SWEPT_FACE",FACE,{"disambiguationData":[OSD([subQ1,subQ0]),TDD([makeQuery(id+"F2.boolean.opBoolean","MERGE",EDGE,{"derivedFrom":[makeQuery(id+"F1.opExtrude","CAP_EDGE",EDGE,{"disambiguationData":[OSD([subQ1])],"isStart":true}),makeQuery(id+"F2.opExtrude","SWEPT_EDGE",EDGE,{"disambiguationData":[OSD([subQ1,subQ0]),TDD([makeQuery(id+"F1.opExtrude","CAP_VERTEX",VERTEX,{"disambiguationData":[OSD([subQ1,subQ0])],"isStart":true})])]})]})])]})]}),makeQuery(id+"F20.opExtrude","SWEPT_FACE",FACE,{"disambiguationData":[OSD([subQ1,subQ0])]})]}),makeQuery(id+"F22.opExtrude","SWEPT_FACE",FACE,{"disambiguationData":[OSD([subQ1,subQ0])]})]}),makeQuery(id+"F24.opExtrude","SWEPT_FACE",FACE,{"disambiguationData":[OSD([subQ1,subQ0])]})]});}
            chamfer(context, id + "F26", {"entities" : qUnion([Q0, Q1, Q2, Q3, Q4, Q5, Q6]), "width" : 1 * mm, "tangentPropagation" : true});
        }
    });
